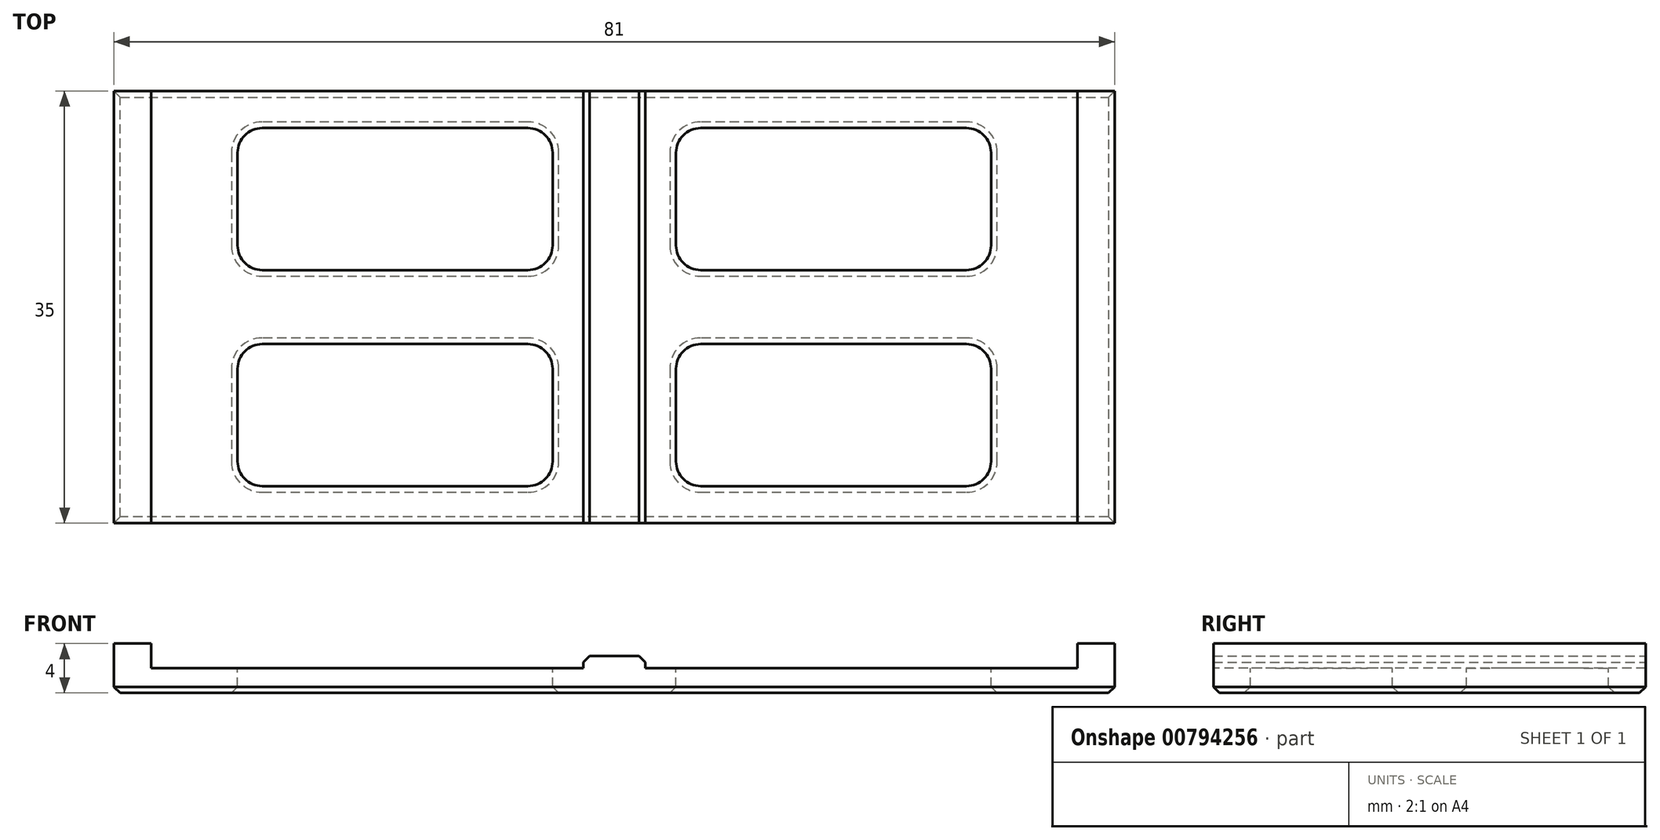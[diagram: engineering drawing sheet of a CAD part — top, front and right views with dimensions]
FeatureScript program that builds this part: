
annotation { "Feature Type Name" : "Feature", "Feature Type Description" : "" }
export const myFeature = defineFeature(function(context is Context, id is Id, definition is map)
    precondition{}
    {
        {
            var Q0;
            Q0=qCreatedBy(makeId("Top.planeOp"),FACE);
            var sketch = newSketch(context, id + "F0", { "sketchPlane" : qUnion([Q0])});
            skLineSegment(sketch, "E0.bottom", {"start": v(-40.5, 17.5) * mm, "end": v(40.5, 17.5) * mm});
            skLineSegment(sketch, "E0.top", {"start": v(-40.5, -17.5) * mm, "end": v(40.5, -17.5) * mm});
            skLineSegment(sketch, "E0.left", {"start": v(-40.5, 17.5) * mm, "end": v(-40.5, -17.5) * mm});
            skLineSegment(sketch, "E0.right", {"start": v(40.5, 17.5) * mm, "end": v(40.5, -17.5) * mm});
            skLineSegment(sketch, "E1", {"start": v(0, 17.5) * mm, "end": v(0, -17.5) * mm, "construction": true});
            skLineSegment(sketch, "E2", {"start": v(-40.5, 0) * mm, "end": v(40.5, 0) * mm, "construction": true});
            skPoint(sketch, "E3", {"position": v(0, 0) * mm});
            skSolve(sketch);
        }
        {
            var Q0;
            Q0=makeQuery(id+"F0.imprint","IMPRINT",FACE,{"disambiguationData":[TD([[makeQuery(id+"F0.imprint","IMPRINT",EDGE,{"derivedFrom":sQuery(id+"F0.wireOp",EDGE,"E0.bottom")}),-1.0]])]});
            extrude(context, id + "F1", {"entities" : qUnion([Q0]), "depth" : 2 * mm, "offsetDistance" : 25 * mm});
        }
        {
            var Q0;
            Q0=makeQuery(id+"F1.opExtrude","CAP_FACE",FACE,{"disambiguationData":[OSD([sQuery(id+"F0.wireOp",EDGE,"E0.bottom"),sQuery(id+"F0.wireOp",EDGE,"E0.top"),sQuery(id+"F0.wireOp",EDGE,"E0.left"),sQuery(id+"F0.wireOp",EDGE,"E0.right")])],"isStart":false});
            var sketch = newSketch(context, id + "F2", { "sketchPlane" : qUnion([Q0])});
            skLineSegment(sketch, "E4.bottom", {"start": v(-2.5, -17.5) * mm, "end": v(2.5, -17.5) * mm});
            skLineSegment(sketch, "E4.top", {"start": v(-2.5, 17.5) * mm, "end": v(2.5, 17.5) * mm});
            skLineSegment(sketch, "E4.left", {"start": v(-2.5, -17.5) * mm, "end": v(-2.5, 17.5) * mm});
            skLineSegment(sketch, "E4.right", {"start": v(2.5, -17.5) * mm, "end": v(2.5, 17.5) * mm});
            skPoint(sketch, "E4.middle", {"position": v(0, 0) * mm});
            skSolve(sketch);
        }
        {
            var Q0;
            Q0=makeQuery(id+"F2.imprint","IMPRINT",FACE,{"disambiguationData":[TD([[makeQuery(id+"F2.imprint","IMPRINT",EDGE,{"derivedFrom":sQuery(id+"F2.wireOp",EDGE,"E4.bottom")}),1.0]])]});
            extrude(context, id + "F3", {"entities" : qUnion([Q0]), "operationType" : NewBodyOperationType.ADD, "depth" : 1 * mm, "offsetDistance" : 25 * mm});
        }
        {
            var Q0;
            {var subQ0=sQuery(id+"F0.wireOp",EDGE,"E0.left");var subQ1=sQuery(id+"F0.wireOp",EDGE,"E0.top");var subQ2=sQuery(id+"F0.wireOp",EDGE,"E0.bottom");Q0=makeQuery(id+"F3.boolean.opBoolean","SPLIT",FACE,{"disambiguationData":[TD([makeQuery(id+"F1.opExtrude","SWEPT_FACE",FACE,{"disambiguationData":[OSD([subQ0])]})])],"derivedFrom":makeQuery(id+"F1.opExtrude","CAP_FACE",FACE,{"disambiguationData":[OSD([subQ2,subQ1,subQ0,sQuery(id+"F0.wireOp",EDGE,"E0.right")])],"isStart":false})});}
            var sketch = newSketch(context, id + "F4", { "sketchPlane" : qUnion([Q0])});
            skLineSegment(sketch, "E5.bottom", {"start": v(-40.5, 17.5) * mm, "end": v(-37.5, 17.5) * mm});
            skLineSegment(sketch, "E5.top", {"start": v(-40.5, -17.5) * mm, "end": v(-37.5, -17.5) * mm});
            skLineSegment(sketch, "E5.left", {"start": v(-40.5, 17.5) * mm, "end": v(-40.5, -17.5) * mm});
            skLineSegment(sketch, "E5.right", {"start": v(-37.5, 17.5) * mm, "end": v(-37.5, -17.5) * mm});
            skLineSegment(sketch, "E6.bottom", {"start": v(40.5, 17.5) * mm, "end": v(37.5, 17.5) * mm});
            skLineSegment(sketch, "E6.top", {"start": v(40.5, -17.5) * mm, "end": v(37.5, -17.5) * mm});
            skLineSegment(sketch, "E6.left", {"start": v(40.5, 17.5) * mm, "end": v(40.5, -17.5) * mm});
            skLineSegment(sketch, "E6.right", {"start": v(37.5, 17.5) * mm, "end": v(37.5, -17.5) * mm});
            skSolve(sketch);
        }
        {
            var Q0;
            Q0=makeQuery(id+"F4.imprint","IMPRINT",FACE,{"disambiguationData":[TD([[makeQuery(id+"F4.imprint","IMPRINT",EDGE,{"derivedFrom":sQuery(id+"F4.wireOp",EDGE,"E5.bottom")}),-1.0]])]});
            var Q1;
            Q1=makeQuery(id+"F4.imprint","IMPRINT",FACE,{"disambiguationData":[TD([[makeQuery(id+"F4.imprint","IMPRINT",EDGE,{"derivedFrom":sQuery(id+"F4.wireOp",EDGE,"E6.bottom")}),1.0]])]});
            extrude(context, id + "F5", {"entities" : qUnion([Q0, Q1]), "operationType" : NewBodyOperationType.ADD, "depth" : 2 * mm, "offsetDistance" : 25 * mm});
        }
        {
            var Q0;
            {var subQ0=sQuery(id+"F0.wireOp",EDGE,"E0.left");var subQ1=sQuery(id+"F0.wireOp",EDGE,"E0.top");var subQ2=sQuery(id+"F0.wireOp",EDGE,"E0.bottom");Q0=makeQuery(id+"F3.boolean.opBoolean","SPLIT",FACE,{"disambiguationData":[TD([makeQuery(id+"F1.opExtrude","SWEPT_FACE",FACE,{"disambiguationData":[OSD([subQ0])]})])],"derivedFrom":makeQuery(id+"F1.opExtrude","CAP_FACE",FACE,{"disambiguationData":[OSD([subQ2,subQ1,subQ0,sQuery(id+"F0.wireOp",EDGE,"E0.right")])],"isStart":false})});}
            var sketch = newSketch(context, id + "F6", { "sketchPlane" : qUnion([Q0])});
            skLineSegment(sketch, "E7", {"start": v(0, 18.55) * mm, "end": v(0, -19.79) * mm, "construction": true});
            skLineSegment(sketch, "E8", {"start": v(-44.93, 0) * mm, "end": v(47.59, 0) * mm, "construction": true});
            skLineSegment(sketch, "E9.bottom", {"start": v(-28.5, 14.5) * mm, "end": v(-7, 14.5) * mm});
            skLineSegment(sketch, "E9.top", {"start": v(-28.5, 3) * mm, "end": v(-7, 3) * mm});
            skLineSegment(sketch, "E9.left", {"start": v(-30.5, 12.5) * mm, "end": v(-30.5, 5) * mm});
            skLineSegment(sketch, "E9.right", {"start": v(-5, 12.5) * mm, "end": v(-5, 5) * mm});
            skPoint(sketch, "E10.visualSharp", {"position": v(-30.5, 14.5) * mm});
            skArc(sketch, "E10.filletArc", {"start": v(-28.5, 14.5) * mm, "mid": v(-29.91, 13.91) * mm, "end": v(-30.5, 12.5) * mm});
            skPoint(sketch, "E11.visualSharp", {"position": v(-5, 14.5) * mm});
            skArc(sketch, "E11.filletArc", {"start": v(-5, 12.5) * mm, "mid": v(-5.59, 13.91) * mm, "end": v(-7, 14.5) * mm});
            skPoint(sketch, "E12.visualSharp", {"position": v(-5, 3) * mm});
            skArc(sketch, "E12.filletArc", {"start": v(-7, 3) * mm, "mid": v(-5.59, 3.59) * mm, "end": v(-5, 5) * mm});
            skPoint(sketch, "E13.visualSharp", {"position": v(-30.5, 3) * mm});
            skArc(sketch, "E13.filletArc", {"start": v(-30.5, 5) * mm, "mid": v(-29.91, 3.59) * mm, "end": v(-28.5, 3) * mm});
            skLineSegment(sketch, "E14.MirrorCS", {"start": v(-30.5, -12.5) * mm, "end": v(-30.5, -5) * mm});
            skArc(sketch, "E15.MirrorCS", {"start": v(-28.5, -14.5) * mm, "mid": v(-29.91, -13.91) * mm, "end": v(-30.5, -12.5) * mm});
            skLineSegment(sketch, "E16.MirrorCS", {"start": v(-28.5, -14.5) * mm, "end": v(-7, -14.5) * mm});
            skArc(sketch, "E17.MirrorCS", {"start": v(-5, -12.5) * mm, "mid": v(-5.59, -13.91) * mm, "end": v(-7, -14.5) * mm});
            skLineSegment(sketch, "E18.MirrorCS", {"start": v(-5, -12.5) * mm, "end": v(-5, -5) * mm});
            skArc(sketch, "E19.MirrorCS", {"start": v(-7, -3) * mm, "mid": v(-5.59, -3.59) * mm, "end": v(-5, -5) * mm});
            skLineSegment(sketch, "E20.MirrorCS", {"start": v(-28.5, -3) * mm, "end": v(-7, -3) * mm});
            skArc(sketch, "E21.MirrorCS", {"start": v(-30.5, -5) * mm, "mid": v(-29.91, -3.59) * mm, "end": v(-28.5, -3) * mm});
            skArc(sketch, "E22.MirrorCS", {"start": v(5, 12.5) * mm, "mid": v(5.59, 13.91) * mm, "end": v(7, 14.5) * mm});
            skArc(sketch, "E23.MirrorCS", {"start": v(7, 3) * mm, "mid": v(5.59, 3.59) * mm, "end": v(5, 5) * mm});
            skArc(sketch, "E24.MirrorCS", {"start": v(28.5, 14.5) * mm, "mid": v(29.91, 13.91) * mm, "end": v(30.5, 12.5) * mm});
            skArc(sketch, "E25.MirrorCS", {"start": v(30.5, 5) * mm, "mid": v(29.91, 3.59) * mm, "end": v(28.5, 3) * mm});
            skLineSegment(sketch, "E26.MirrorCS", {"start": v(5, 12.5) * mm, "end": v(5, 5) * mm});
            skLineSegment(sketch, "E27.MirrorCS", {"start": v(30.5, 12.5) * mm, "end": v(30.5, 5) * mm});
            skLineSegment(sketch, "E28.MirrorCS", {"start": v(28.5, 3) * mm, "end": v(7, 3) * mm});
            skLineSegment(sketch, "E29.MirrorCS", {"start": v(28.5, 14.5) * mm, "end": v(7, 14.5) * mm});
            skPoint(sketch, "E30.MirrorP", {"position": v(30.5, 14.5) * mm});
            skPoint(sketch, "E31.MirrorP", {"position": v(5, 14.5) * mm});
            skPoint(sketch, "E32.MirrorP", {"position": v(5, 3) * mm});
            skPoint(sketch, "E33.MirrorP", {"position": v(30.5, 3) * mm});
            skArc(sketch, "E34.MirrorCS", {"start": v(7, -3) * mm, "mid": v(5.59, -3.59) * mm, "end": v(5, -5) * mm});
            skLineSegment(sketch, "E35.MirrorCS", {"start": v(5, -12.5) * mm, "end": v(5, -5) * mm});
            skArc(sketch, "E36.MirrorCS", {"start": v(5, -12.5) * mm, "mid": v(5.59, -13.91) * mm, "end": v(7, -14.5) * mm});
            skLineSegment(sketch, "E37.MirrorCS", {"start": v(28.5, -3) * mm, "end": v(7, -3) * mm});
            skLineSegment(sketch, "E38.MirrorCS", {"start": v(30.5, -12.5) * mm, "end": v(30.5, -5) * mm});
            skArc(sketch, "E39.MirrorCS", {"start": v(28.5, -14.5) * mm, "mid": v(29.91, -13.91) * mm, "end": v(30.5, -12.5) * mm});
            skLineSegment(sketch, "E40.MirrorCS", {"start": v(28.5, -14.5) * mm, "end": v(7, -14.5) * mm});
            skArc(sketch, "E41.MirrorCS", {"start": v(30.5, -5) * mm, "mid": v(29.91, -3.59) * mm, "end": v(28.5, -3) * mm});
            skSolve(sketch);
        }
        {
            var Q0;
            Q0 = qSketchRegion(id + "F6", true);
            extrude(context, id + "F7", {"entities" : qUnion([Q0]), "operationType" : NewBodyOperationType.REMOVE, "endBound" : BoundingType.THROUGH_ALL, "oppositeDirection" : true, "depth" : 25 * mm, "offsetDistance" : 25 * mm});
        }
        {
            var Q0;
            Q0=makeQuery(id+"F1.opExtrude","CAP_EDGE",EDGE,{"disambiguationData":[OSD([sQuery(id+"F0.wireOp",EDGE,"E0.top")])],"isStart":true});
            var Q1;
            Q1=makeQuery(id+"F1.opExtrude","CAP_EDGE",EDGE,{"disambiguationData":[OSD([sQuery(id+"F0.wireOp",EDGE,"E0.right")])],"isStart":true});
            var Q2;
            Q2=makeQuery(id+"F1.opExtrude","CAP_EDGE",EDGE,{"disambiguationData":[OSD([sQuery(id+"F0.wireOp",EDGE,"E0.bottom")])],"isStart":true});
            var Q3;
            Q3=makeQuery(id+"F1.opExtrude","CAP_EDGE",EDGE,{"disambiguationData":[OSD([sQuery(id+"F0.wireOp",EDGE,"E0.left")])],"isStart":true});
            chamfer(context, id + "F8", {"entities" : qUnion([Q0, Q1, Q2, Q3]), "width" : .5 * mm, "tangentPropagation" : true});
        }
        {
            var Q0;
            Q0=makeQuery(id+"F3.opExtrude","CAP_EDGE",EDGE,{"disambiguationData":[OSD([sQuery(id+"F2.wireOp",EDGE,"E4.right")])],"isStart":false});
            var Q1;
            Q1=makeQuery(id+"F3.opExtrude","CAP_EDGE",EDGE,{"disambiguationData":[OSD([sQuery(id+"F2.wireOp",EDGE,"E4.left")])],"isStart":false});
            var Q2;
            Q2=makeQuery(id+"F7.boolean.opBoolean","COPY",EDGE,{"derivedFrom":makeQuery(id+"F7.opExtrude","CAP_EDGE",EDGE,{"disambiguationData":[OSD([sQuery(id+"F6.wireOp",EDGE,"E40.MirrorCS")])],"isStart":true})});
            var Q3;
            Q3=makeQuery(id+"F7.boolean.opBoolean","COPY",EDGE,{"derivedFrom":makeQuery(id+"F7.opExtrude","CAP_EDGE",EDGE,{"disambiguationData":[OSD([sQuery(id+"F6.wireOp",EDGE,"E28.MirrorCS")])],"isStart":true})});
            var Q4;
            Q4=makeQuery(id+"F7.boolean.opBoolean","COPY",EDGE,{"derivedFrom":makeQuery(id+"F7.opExtrude","CAP_EDGE",EDGE,{"disambiguationData":[OSD([sQuery(id+"F6.wireOp",EDGE,"E20.MirrorCS")])],"isStart":true})});
            var Q5;
            Q5=makeQuery(id+"F7.boolean.opBoolean","COPY",EDGE,{"derivedFrom":makeQuery(id+"F7.opExtrude","CAP_EDGE",EDGE,{"disambiguationData":[OSD([sQuery(id+"F6.wireOp",EDGE,"E9.top")])],"isStart":true})});
            var Q6;
            Q6=makeQuery(id+"F7.boolean.opBoolean","INTERSECT",EDGE,{"derivedFrom":[makeQuery(id+"F1.opExtrude","CAP_FACE",FACE,{"disambiguationData":[OSD([sQuery(id+"F0.wireOp",EDGE,"E0.bottom"),sQuery(id+"F0.wireOp",EDGE,"E0.top"),sQuery(id+"F0.wireOp",EDGE,"E0.left"),sQuery(id+"F0.wireOp",EDGE,"E0.right")])],"isStart":true}),makeQuery(id+"F7.opExtrude","SWEPT_FACE",FACE,{"disambiguationData":[OSD([sQuery(id+"F6.wireOp",EDGE,"E20.MirrorCS")])]})]});
            var Q7;
            Q7=makeQuery(id+"F7.boolean.opBoolean","INTERSECT",EDGE,{"derivedFrom":[makeQuery(id+"F1.opExtrude","CAP_FACE",FACE,{"disambiguationData":[OSD([sQuery(id+"F0.wireOp",EDGE,"E0.bottom"),sQuery(id+"F0.wireOp",EDGE,"E0.top"),sQuery(id+"F0.wireOp",EDGE,"E0.left"),sQuery(id+"F0.wireOp",EDGE,"E0.right")])],"isStart":true}),makeQuery(id+"F7.opExtrude","SWEPT_FACE",FACE,{"disambiguationData":[OSD([sQuery(id+"F6.wireOp",EDGE,"E9.bottom")])]})]});
            var Q8;
            Q8=makeQuery(id+"F7.boolean.opBoolean","INTERSECT",EDGE,{"derivedFrom":[makeQuery(id+"F1.opExtrude","CAP_FACE",FACE,{"disambiguationData":[OSD([sQuery(id+"F0.wireOp",EDGE,"E0.bottom"),sQuery(id+"F0.wireOp",EDGE,"E0.top"),sQuery(id+"F0.wireOp",EDGE,"E0.left"),sQuery(id+"F0.wireOp",EDGE,"E0.right")])],"isStart":true}),makeQuery(id+"F7.opExtrude","SWEPT_FACE",FACE,{"disambiguationData":[OSD([sQuery(id+"F6.wireOp",EDGE,"E29.MirrorCS")])]})]});
            var Q9;
            Q9=makeQuery(id+"F7.boolean.opBoolean","INTERSECT",EDGE,{"derivedFrom":[makeQuery(id+"F1.opExtrude","CAP_FACE",FACE,{"disambiguationData":[OSD([sQuery(id+"F0.wireOp",EDGE,"E0.bottom"),sQuery(id+"F0.wireOp",EDGE,"E0.top"),sQuery(id+"F0.wireOp",EDGE,"E0.left"),sQuery(id+"F0.wireOp",EDGE,"E0.right")])],"isStart":true}),makeQuery(id+"F7.opExtrude","SWEPT_FACE",FACE,{"disambiguationData":[OSD([sQuery(id+"F6.wireOp",EDGE,"E37.MirrorCS")])]})]});
            chamfer(context, id + "F9", {"entities" : qUnion([Q0, Q1, Q2, Q3, Q4, Q5, Q6, Q7, Q8, Q9]), "width" : .5 * mm, "tangentPropagation" : true});
        }
    });
